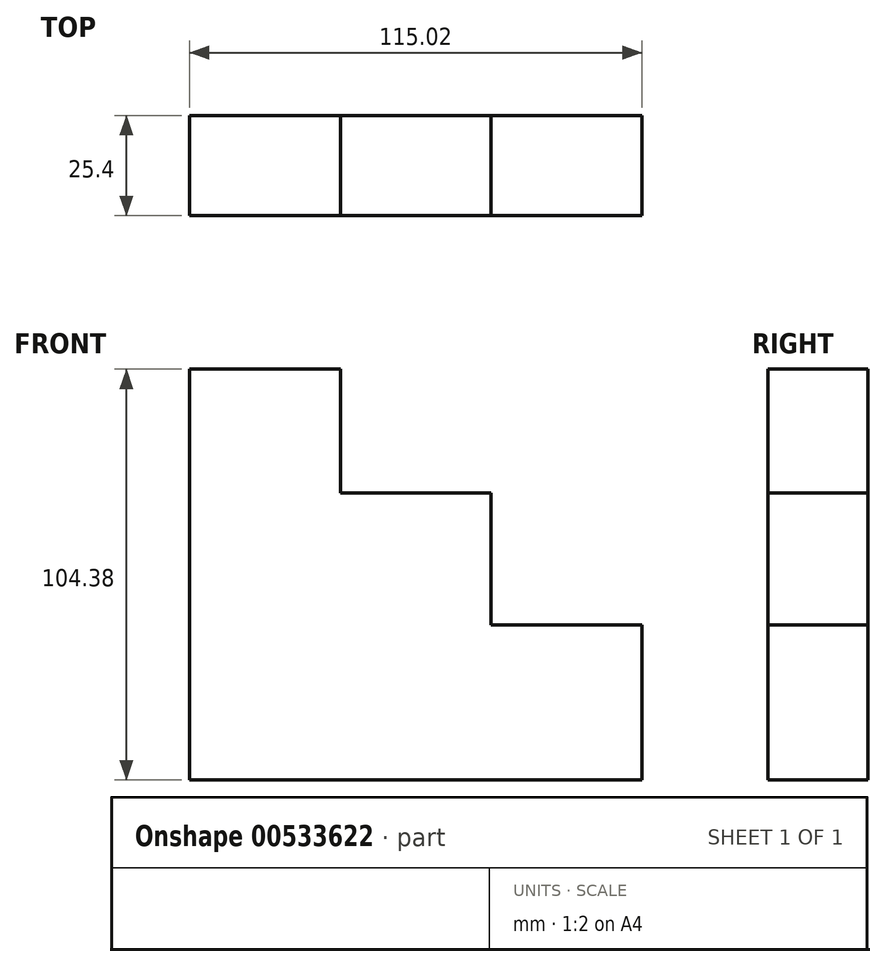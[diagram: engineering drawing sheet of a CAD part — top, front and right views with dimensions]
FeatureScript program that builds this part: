
annotation { "Feature Type Name" : "Feature", "Feature Type Description" : "" }
export const myFeature = defineFeature(function(context is Context, id is Id, definition is map)
    precondition{}
    {
        {
            var Q0;
            Q0=qCreatedBy(makeId("Front.planeOp"),FACE);
            var sketch = newSketch(context, id + "F0", { "sketchPlane" : qUnion([Q0])});
            skLineSegment(sketch, "E0", {"start": v(0, 0) * mm, "end": v(115.02, 0) * mm});
            skLineSegment(sketch, "E1", {"start": v(115.02, 0) * mm, "end": v(115.02, 39.35) * mm});
            skLineSegment(sketch, "E2", {"start": v(115.02, 39.35) * mm, "end": v(76.68, 39.35) * mm});
            skLineSegment(sketch, "E3", {"start": v(76.68, 39.35) * mm, "end": v(76.68, 72.9) * mm});
            skLineSegment(sketch, "E4", {"start": v(76.68, 72.9) * mm, "end": v(38.34, 72.9) * mm});
            skLineSegment(sketch, "E5", {"start": v(38.34, 72.9) * mm, "end": v(38.34, 104.38) * mm});
            skLineSegment(sketch, "E6", {"start": v(38.34, 104.38) * mm, "end": v(0, 104.38) * mm});
            skLineSegment(sketch, "E7", {"start": v(0, 104.38) * mm, "end": v(0, 0) * mm});
            skSolve(sketch);
        }
        {
            var Q0;
            Q0=makeQuery(id+"F0.imprint","IMPRINT",FACE,{"disambiguationData":[TD([[makeQuery(id+"F0.imprint","IMPRINT",EDGE,{"derivedFrom":sQuery(id+"F0.wireOp",EDGE,"E0")}),1.0]])]});
            extrude(context, id + "F1", {"entities" : qUnion([Q0]), "depth" : 25.4 * mm, "offsetDistance" : 25.4 * mm});
        }
    });
